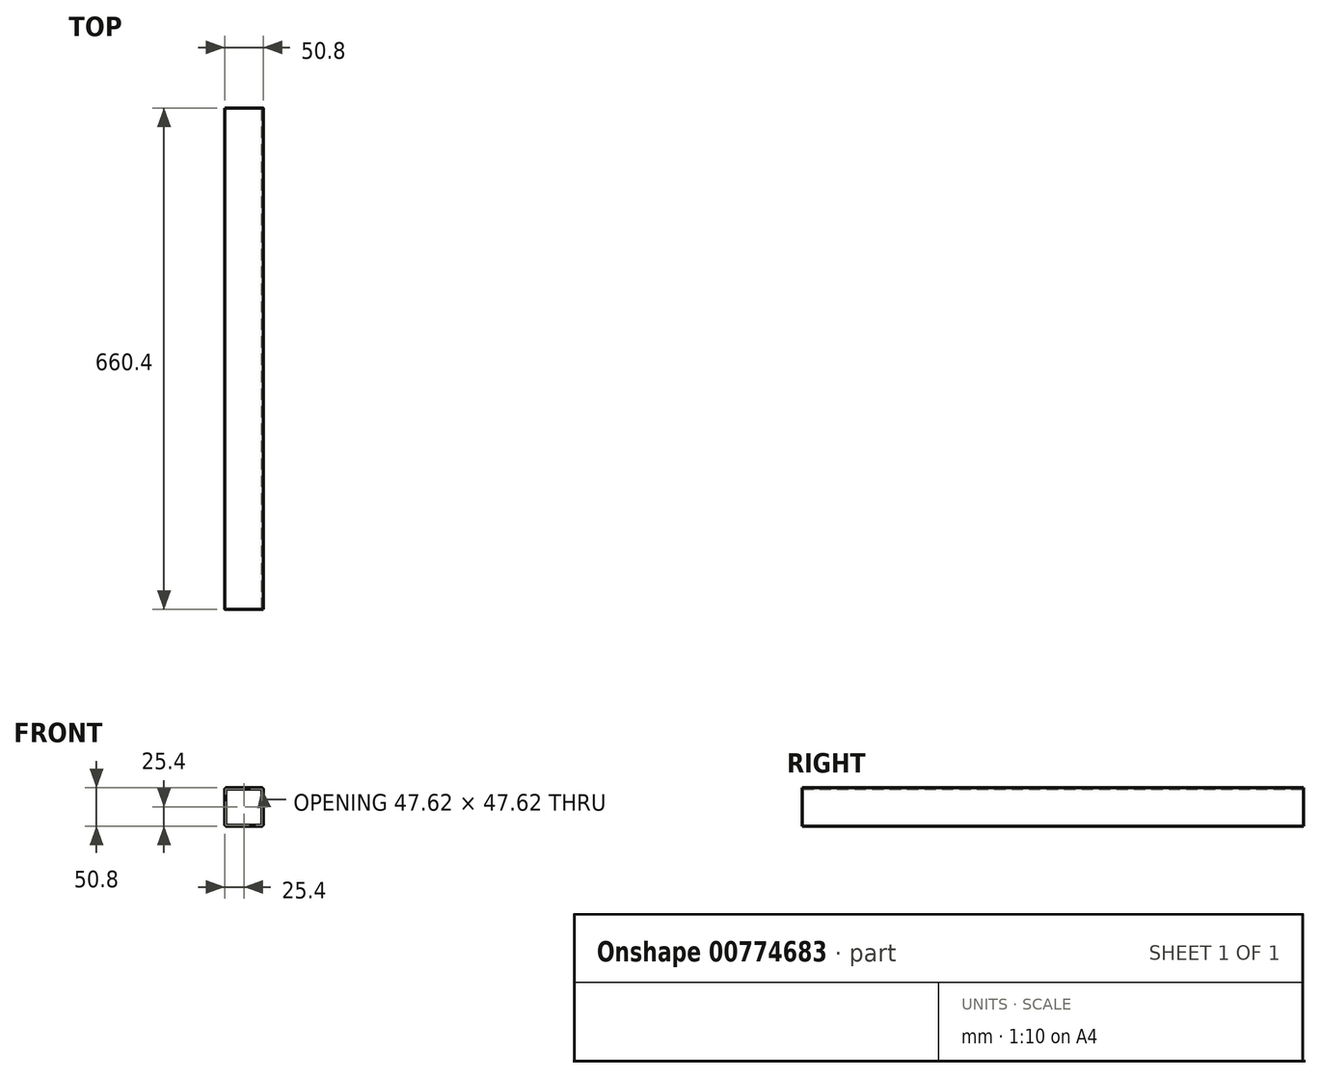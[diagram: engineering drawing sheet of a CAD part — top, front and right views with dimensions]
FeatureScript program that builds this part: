
annotation { "Feature Type Name" : "Feature", "Feature Type Description" : "" }
export const myFeature = defineFeature(function(context is Context, id is Id, definition is map)
    precondition{}
    {
        {
            var Q0;
            Q0=qCreatedBy(makeId("Front.planeOp"),FACE);
            var sketch = newSketch(context, id + "F0", { "sketchPlane" : qUnion([Q0])});
            skLineSegment(sketch, "E0.bottom", {"start": v(22.86, -25.4) * mm, "end": v(-22.86, -25.4) * mm});
            skLineSegment(sketch, "E0.top", {"start": v(22.86, 25.4) * mm, "end": v(-22.86, 25.4) * mm});
            skLineSegment(sketch, "E0.left", {"start": v(25.4, -22.86) * mm, "end": v(25.4, 22.86) * mm});
            skLineSegment(sketch, "E0.right", {"start": v(-25.4, -22.86) * mm, "end": v(-25.4, 22.86) * mm});
            skPoint(sketch, "E0.middle", {"position": v(0, 0) * mm});
            skLineSegment(sketch, "E1.bottom", {"start": v(22.54, -23.81) * mm, "end": v(-22.54, -23.81) * mm});
            skLineSegment(sketch, "E1.top", {"start": v(22.54, 23.81) * mm, "end": v(-22.54, 23.81) * mm});
            skLineSegment(sketch, "E1.left", {"start": v(23.81, -22.54) * mm, "end": v(23.81, 22.54) * mm});
            skLineSegment(sketch, "E1.right", {"start": v(-23.81, -22.54) * mm, "end": v(-23.81, 22.54) * mm});
            skPoint(sketch, "E2.visualSharp", {"position": v(25.4, 25.4) * mm});
            skArc(sketch, "E2.filletArc", {"start": v(25.4, 22.86) * mm, "mid": v(24.66, 24.66) * mm, "end": v(22.86, 25.4) * mm});
            skPoint(sketch, "E3.visualSharp", {"position": v(25.4, -25.4) * mm});
            skArc(sketch, "E3.filletArc", {"start": v(22.86, -25.4) * mm, "mid": v(24.66, -24.66) * mm, "end": v(25.4, -22.86) * mm});
            skPoint(sketch, "E4.visualSharp", {"position": v(-25.4, -25.4) * mm});
            skArc(sketch, "E4.filletArc", {"start": v(-25.4, -22.86) * mm, "mid": v(-24.66, -24.66) * mm, "end": v(-22.86, -25.4) * mm});
            skPoint(sketch, "E5.visualSharp", {"position": v(-25.4, 25.4) * mm});
            skArc(sketch, "E5.filletArc", {"start": v(-22.86, 25.4) * mm, "mid": v(-24.66, 24.66) * mm, "end": v(-25.4, 22.86) * mm});
            skPoint(sketch, "E6.visualSharp", {"position": v(-23.81, 23.81) * mm});
            skArc(sketch, "E6.filletArc", {"start": v(-22.54, 23.81) * mm, "mid": v(-23.44, 23.44) * mm, "end": v(-23.81, 22.54) * mm});
            skPoint(sketch, "E7.visualSharp", {"position": v(23.81, 23.81) * mm});
            skArc(sketch, "E7.filletArc", {"start": v(23.81, 22.54) * mm, "mid": v(23.44, 23.44) * mm, "end": v(22.54, 23.81) * mm});
            skPoint(sketch, "E8.visualSharp", {"position": v(23.81, -23.81) * mm});
            skArc(sketch, "E8.filletArc", {"start": v(22.54, -23.81) * mm, "mid": v(23.44, -23.44) * mm, "end": v(23.81, -22.54) * mm});
            skPoint(sketch, "E9.visualSharp", {"position": v(-23.81, -23.81) * mm});
            skArc(sketch, "E9.filletArc", {"start": v(-23.81, -22.54) * mm, "mid": v(-23.44, -23.44) * mm, "end": v(-22.54, -23.81) * mm});
            skSolve(sketch);
        }
        {
            var Q0;
            Q0=makeQuery(id+"F0.imprint","IMPRINT",FACE,{"disambiguationData":[TD([[makeQuery(id+"F0.imprint","IMPRINT",EDGE,{"derivedFrom":sQuery(id+"F0.wireOp",EDGE,"E0.bottom")}),-1.0]])]});
            extrude(context, id + "F1", {"entities" : qUnion([Q0]), "depth" : 660.4 * mm, "offsetDistance" : 25.4 * mm});
        }
    });
